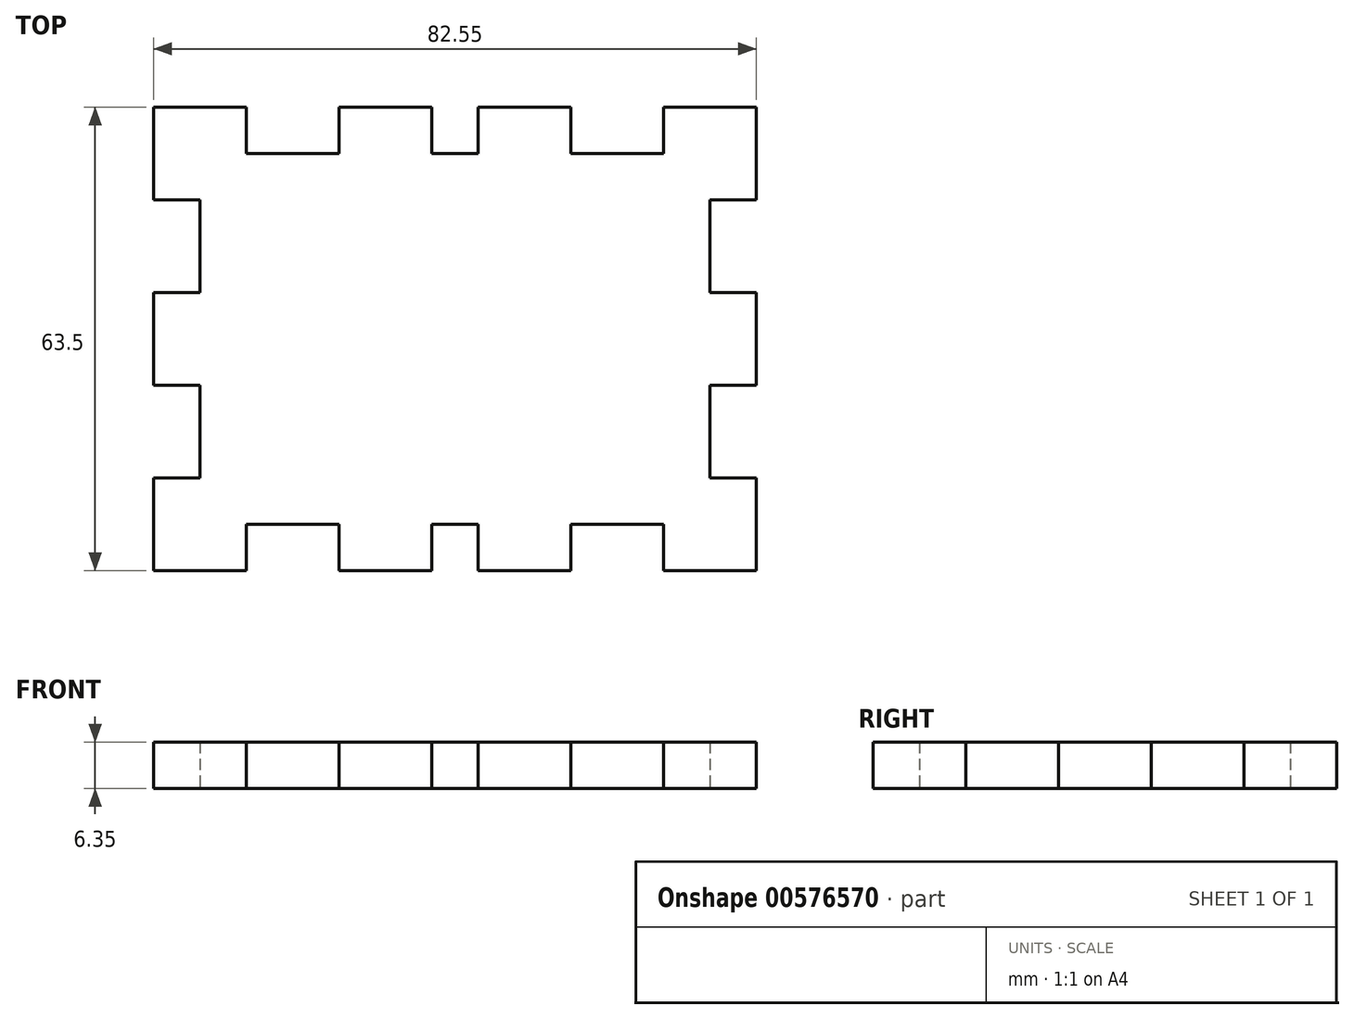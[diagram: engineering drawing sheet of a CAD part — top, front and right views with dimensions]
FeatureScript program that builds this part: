
annotation { "Feature Type Name" : "Feature", "Feature Type Description" : "" }
export const myFeature = defineFeature(function(context is Context, id is Id, definition is map)
    precondition{}
    {
        {
            var Q0;
            Q0=qCreatedBy(makeId("Top.planeOp"),FACE);
            var sketch = newSketch(context, id + "F0", { "sketchPlane" : qUnion([Q0])});
            skLineSegment(sketch, "E0.bottom", {"start": v(0, 0) * mm, "end": v(12.7, 0) * mm});
            skLineSegment(sketch, "E0.left", {"start": v(0, 0) * mm, "end": v(0, -12.7) * mm});
            skLineSegment(sketch, "E1", {"start": v(12.7, 0) * mm, "end": v(12.7, -6.35) * mm});
            skLineSegment(sketch, "E2", {"start": v(12.7, -6.35) * mm, "end": v(25.4, -6.35) * mm});
            skLineSegment(sketch, "E3", {"start": v(25.4, -6.35) * mm, "end": v(25.4, 0) * mm});
            skLineSegment(sketch, "E4", {"start": v(25.4, 0) * mm, "end": v(38.11, 0) * mm});
            skLineSegment(sketch, "E5", {"start": v(38.11, 0) * mm, "end": v(38.11, -6.35) * mm});
            skLineSegment(sketch, "E6", {"start": v(38.11, -6.35) * mm, "end": v(44.44, -6.35) * mm});
            skLineSegment(sketch, "E7", {"start": v(44.44, -6.35) * mm, "end": v(44.44, 0) * mm});
            skLineSegment(sketch, "E8", {"start": v(44.44, 0) * mm, "end": v(57.14, 0) * mm});
            skLineSegment(sketch, "E9", {"start": v(57.14, 0) * mm, "end": v(57.14, -6.35) * mm});
            skLineSegment(sketch, "E10", {"start": v(57.14, -6.35) * mm, "end": v(69.85, -6.35) * mm});
            skLineSegment(sketch, "E11", {"start": v(69.85, -6.35) * mm, "end": v(69.85, 0) * mm});
            skLineSegment(sketch, "E12.trimOffspring", {"start": v(69.85, 0) * mm, "end": v(82.55, 0) * mm});
            skLineSegment(sketch, "E13.bottom", {"start": v(0, 0) * mm, "end": v(0, 0) * mm});
            skLineSegment(sketch, "E13.top", {"start": v(0, -12.7) * mm, "end": v(0, -12.7) * mm});
            skLineSegment(sketch, "E14.bottom", {"start": v(0, -12.7) * mm, "end": v(6.35, -12.7) * mm});
            skLineSegment(sketch, "E14.top", {"start": v(0, -12.7) * mm, "end": v(6.35, -12.7) * mm});
            skLineSegment(sketch, "E14.right", {"start": v(6.35, -12.7) * mm, "end": v(6.35, -12.7) * mm});
            skLineSegment(sketch, "E15", {"start": v(6.35, -12.7) * mm, "end": v(6.35, -25.4) * mm});
            skLineSegment(sketch, "E16", {"start": v(6.35, -25.4) * mm, "end": v(0, -25.4) * mm});
            skLineSegment(sketch, "E17", {"start": v(0, -25.4) * mm, "end": v(0, -38.1) * mm});
            skLineSegment(sketch, "E18", {"start": v(0, -38.1) * mm, "end": v(6.35, -38.1) * mm});
            skLineSegment(sketch, "E19", {"start": v(6.35, -38.1) * mm, "end": v(6.35, -50.8) * mm});
            skLineSegment(sketch, "E20", {"start": v(6.35, -50.8) * mm, "end": v(0, -50.8) * mm});
            skLineSegment(sketch, "E21.trimOffspring", {"start": v(0, -50.8) * mm, "end": v(0, -63.5) * mm});
            skLineSegment(sketch, "E22", {"start": v(41.28, -6.35) * mm, "end": v(41.28, -30.54) * mm, "construction": true});
            skLineSegment(sketch, "E23", {"start": v(0, -31.75) * mm, "end": v(22.37, -31.75) * mm, "construction": true});
            skPoint(sketch, "E23.endSnap0", {"position": v(0, -31.75) * mm});
            skLineSegment(sketch, "E24.MirrorCS", {"start": v(82.55, 0) * mm, "end": v(82.55, -12.7) * mm});
            skLineSegment(sketch, "E25.MirrorCS", {"start": v(82.55, -12.7) * mm, "end": v(76.2, -12.7) * mm});
            skLineSegment(sketch, "E26.MirrorCS", {"start": v(76.2, -12.7) * mm, "end": v(76.2, -25.4) * mm});
            skLineSegment(sketch, "E27.MirrorCS", {"start": v(76.2, -25.4) * mm, "end": v(82.55, -25.4) * mm});
            skLineSegment(sketch, "E28.MirrorCS", {"start": v(82.55, -25.4) * mm, "end": v(82.55, -38.1) * mm});
            skLineSegment(sketch, "E29.MirrorCS", {"start": v(82.55, -38.1) * mm, "end": v(76.2, -38.1) * mm});
            skLineSegment(sketch, "E30.MirrorCS", {"start": v(76.2, -38.1) * mm, "end": v(76.2, -50.8) * mm});
            skLineSegment(sketch, "E31.MirrorCS", {"start": v(82.55, -50.8) * mm, "end": v(82.55, -63.5) * mm});
            skLineSegment(sketch, "E32.MirrorCS", {"start": v(76.2, -50.8) * mm, "end": v(82.55, -50.8) * mm});
            skLineSegment(sketch, "E33.MirrorCS", {"start": v(0, -63.5) * mm, "end": v(12.7, -63.5) * mm});
            skLineSegment(sketch, "E34.MirrorCS", {"start": v(12.7, -63.5) * mm, "end": v(12.7, -57.15) * mm});
            skLineSegment(sketch, "E35.MirrorCS", {"start": v(12.7, -57.15) * mm, "end": v(25.4, -57.15) * mm});
            skLineSegment(sketch, "E36.MirrorCS", {"start": v(25.4, -57.15) * mm, "end": v(25.4, -63.5) * mm});
            skLineSegment(sketch, "E37.MirrorCS", {"start": v(25.4, -63.5) * mm, "end": v(38.11, -63.5) * mm});
            skLineSegment(sketch, "E38.MirrorCS", {"start": v(38.11, -63.5) * mm, "end": v(38.11, -57.15) * mm});
            skLineSegment(sketch, "E39.MirrorCS", {"start": v(38.11, -57.15) * mm, "end": v(44.44, -57.15) * mm});
            skLineSegment(sketch, "E40.MirrorCS", {"start": v(44.44, -57.15) * mm, "end": v(44.44, -63.5) * mm});
            skLineSegment(sketch, "E41.MirrorCS", {"start": v(44.44, -63.5) * mm, "end": v(57.14, -63.5) * mm});
            skLineSegment(sketch, "E42.MirrorCS", {"start": v(57.14, -63.5) * mm, "end": v(57.14, -57.15) * mm});
            skLineSegment(sketch, "E43.MirrorCS", {"start": v(57.14, -57.15) * mm, "end": v(69.85, -57.15) * mm});
            skLineSegment(sketch, "E44.MirrorCS", {"start": v(69.85, -57.15) * mm, "end": v(69.85, -63.5) * mm});
            skLineSegment(sketch, "E45.MirrorCS", {"start": v(69.85, -63.5) * mm, "end": v(82.55, -63.5) * mm});
            skSolve(sketch);
        }
        {
            var Q0;
            Q0=makeQuery(id+"F0.imprint","IMPRINT",FACE,{"disambiguationData":[TD([[makeQuery(id+"F0.imprint","IMPRINT",EDGE,{"derivedFrom":sQuery(id+"F0.wireOp",EDGE,"E0.bottom")}),-1.0]])]});
            extrude(context, id + "F1", {"entities" : qUnion([Q0]), "depth" : 6.35 * mm, "offsetDistance" : 25.4 * mm});
        }
    });
